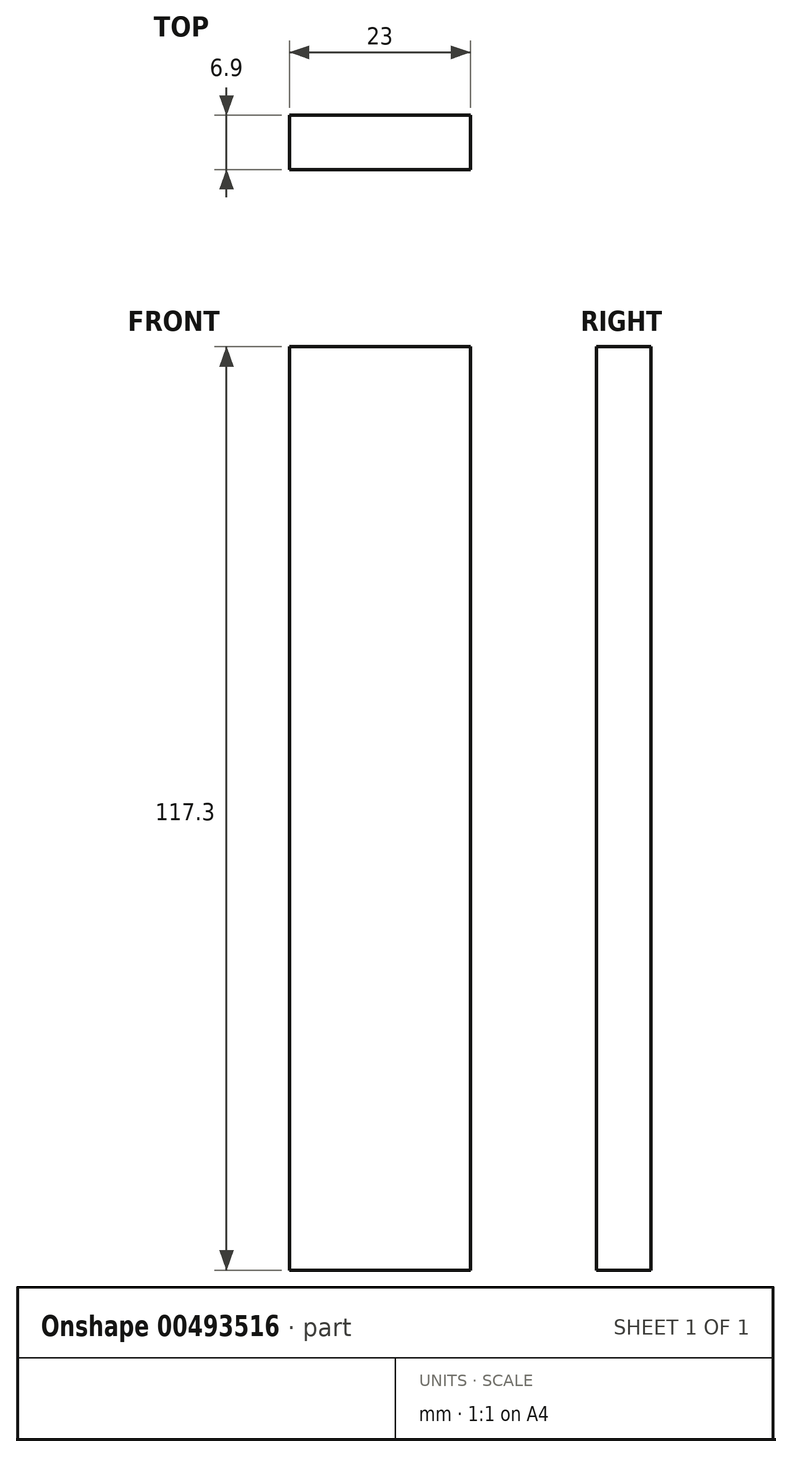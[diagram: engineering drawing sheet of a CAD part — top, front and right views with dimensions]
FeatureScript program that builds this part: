
annotation { "Feature Type Name" : "Feature", "Feature Type Description" : "" }
export const myFeature = defineFeature(function(context is Context, id is Id, definition is map)
    precondition{}
    {
        {
            var Q0;
            Q0=qCreatedBy(makeId("Front.planeOp"),FACE);
            var sketch = newSketch(context, id + "F0", { "sketchPlane" : qUnion([Q0])});
            skLineSegment(sketch, "E0.bottom", {"start": v(-20.1, 76.2) * mm, "end": v(2.9, 76.2) * mm});
            skLineSegment(sketch, "E0.top", {"start": v(-20.1, -41.1) * mm, "end": v(2.9, -41.1) * mm});
            skLineSegment(sketch, "E0.left", {"start": v(-20.1, 76.2) * mm, "end": v(-20.1, -41.1) * mm});
            skLineSegment(sketch, "E0.right", {"start": v(2.9, 76.2) * mm, "end": v(2.9, -41.1) * mm});
            skSolve(sketch);
        }
        {
            var Q0;
            Q0=makeQuery(id+"F0.imprint","IMPRINT",FACE,{"disambiguationData":[TD([[makeQuery(id+"F0.imprint","IMPRINT",EDGE,{"derivedFrom":sQuery(id+"F0.wireOp",EDGE,"E0.bottom")}),-1.0]])]});
            extrude(context, id + "F1", {"entities" : qUnion([Q0]), "depth" : 6.9 * mm});
        }
    });
